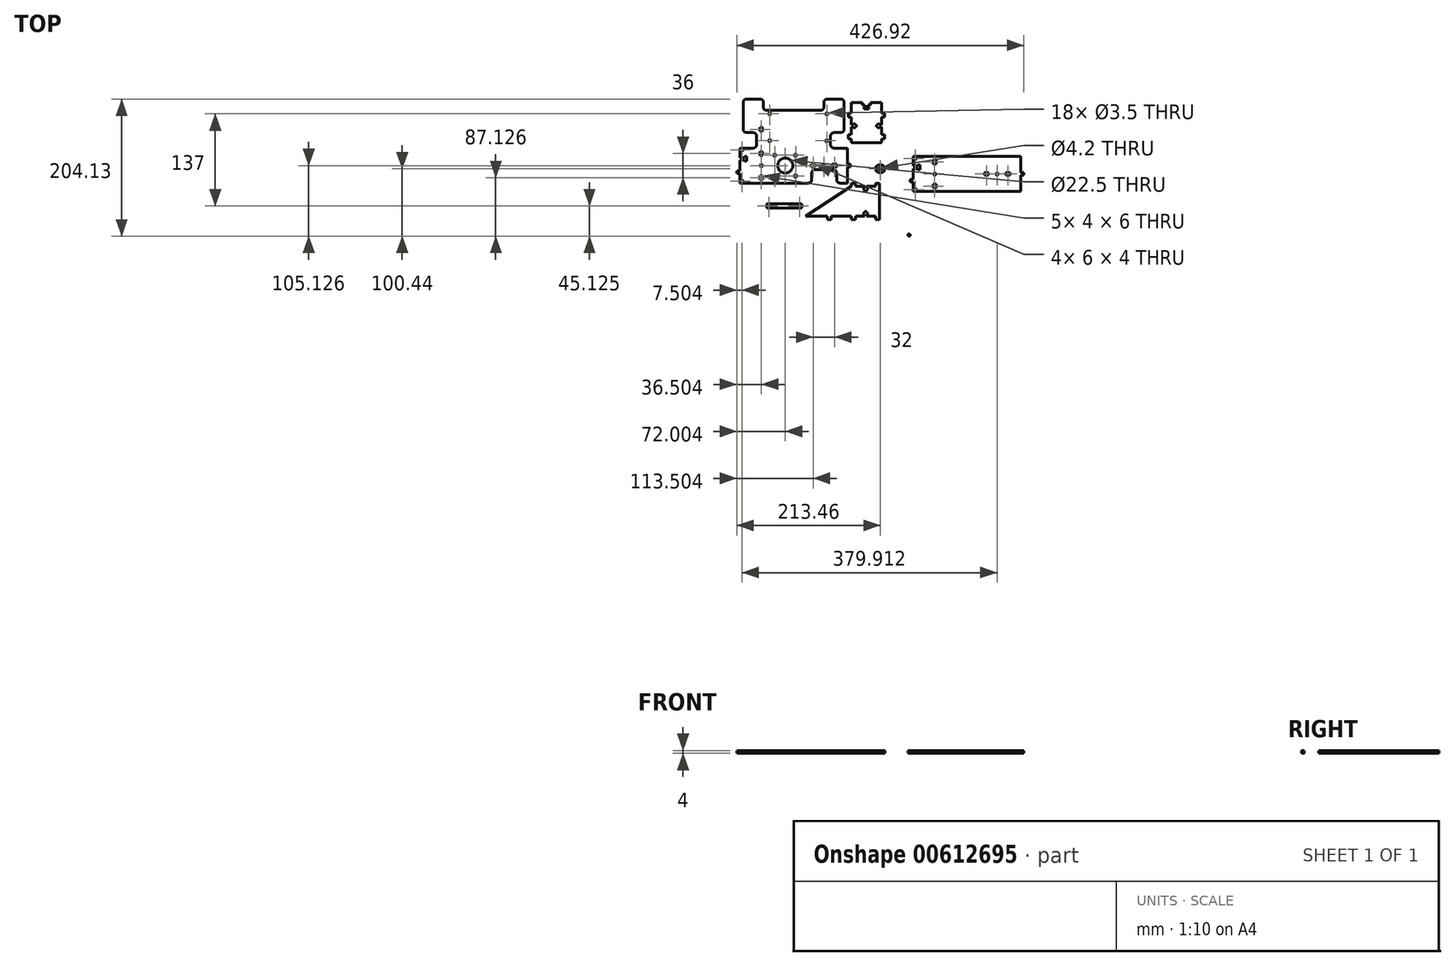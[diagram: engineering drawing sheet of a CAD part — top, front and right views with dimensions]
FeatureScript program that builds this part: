
annotation { "Feature Type Name" : "Feature", "Feature Type Description" : "" }
export const myFeature = defineFeature(function(context is Context, id is Id, definition is map)
    precondition{}
    {
        {
            var Q0;
            Q0=qCreatedBy(makeId("Top.planeOp"),FACE);
            var sketch = newSketch(context, id + "F0", { "sketchPlane" : qUnion([Q0])});
            skLineSegment(sketch, "E0", {"start": v(-0.96, -75.31) * mm, "end": v(-0.96, -21.31) * mm});
            skLineSegment(sketch, "E1", {"start": v(-208.96, 30.69) * mm, "end": v(-188.96, 30.69) * mm});
            skArc(sketch, "E2", {"start": v(-188.96, 30.69) * mm, "mid": v(-185.42, 32.15) * mm, "end": v(-183.96, 35.69) * mm});
            skLineSegment(sketch, "E3", {"start": v(-183.96, 35.69) * mm, "end": v(-183.96, 48.69) * mm});
            skArc(sketch, "E4", {"start": v(-183.96, 48.69) * mm, "mid": v(-185.42, 52.22) * mm, "end": v(-188.96, 53.69) * mm});
            skLineSegment(sketch, "E5", {"start": v(-188.96, 53.69) * mm, "end": v(-198.96, 53.69) * mm});
            skArc(sketch, "E6", {"start": v(-198.96, 53.69) * mm, "mid": v(-202.5, 55.15) * mm, "end": v(-203.96, 58.69) * mm});
            skLineSegment(sketch, "E7", {"start": v(-203.96, 58.69) * mm, "end": v(-203.96, 98.69) * mm});
            skArc(sketch, "E8", {"start": v(-203.96, 98.69) * mm, "mid": v(-202.5, 102.22) * mm, "end": v(-198.96, 103.69) * mm});
            skLineSegment(sketch, "E9", {"start": v(-198.96, 103.69) * mm, "end": v(-178.96, 103.69) * mm});
            skArc(sketch, "E10", {"start": v(-178.96, 103.69) * mm, "mid": v(-175.42, 102.22) * mm, "end": v(-173.96, 98.69) * mm});
            skLineSegment(sketch, "E11", {"start": v(-173.96, 98.69) * mm, "end": v(-173.96, 91.69) * mm});
            skArc(sketch, "E12", {"start": v(-173.96, 91.69) * mm, "mid": v(-172.5, 88.15) * mm, "end": v(-168.96, 86.69) * mm});
            skLineSegment(sketch, "E13", {"start": v(-168.96, 86.69) * mm, "end": v(-88.96, 86.69) * mm});
            skArc(sketch, "E14", {"start": v(-88.96, 86.69) * mm, "mid": v(-85.42, 88.15) * mm, "end": v(-83.96, 91.69) * mm});
            skLineSegment(sketch, "E15", {"start": v(-83.96, 91.69) * mm, "end": v(-83.96, 98.69) * mm});
            skArc(sketch, "E16", {"start": v(-83.96, 98.69) * mm, "mid": v(-82.5, 102.22) * mm, "end": v(-78.96, 103.69) * mm});
            skLineSegment(sketch, "E17", {"start": v(-78.96, 103.69) * mm, "end": v(-58.96, 103.69) * mm});
            skArc(sketch, "E18", {"start": v(-58.96, 103.69) * mm, "mid": v(-55.42, 102.22) * mm, "end": v(-53.96, 98.69) * mm});
            skLineSegment(sketch, "E19", {"start": v(-53.96, 98.69) * mm, "end": v(-53.96, 58.69) * mm});
            skArc(sketch, "E20", {"start": v(-53.96, 58.69) * mm, "mid": v(-55.42, 55.15) * mm, "end": v(-58.96, 53.69) * mm});
            skLineSegment(sketch, "E21", {"start": v(-58.96, 53.69) * mm, "end": v(-68.96, 53.69) * mm});
            skArc(sketch, "E22", {"start": v(-68.96, 53.69) * mm, "mid": v(-72.5, 52.22) * mm, "end": v(-73.96, 48.69) * mm});
            skLineSegment(sketch, "E23", {"start": v(-73.96, 48.69) * mm, "end": v(-73.96, 35.69) * mm});
            skArc(sketch, "E24", {"start": v(-73.96, 35.69) * mm, "mid": v(-72.5, 32.15) * mm, "end": v(-68.96, 30.69) * mm});
            skLineSegment(sketch, "E25", {"start": v(-68.96, 30.69) * mm, "end": v(-48.96, 30.69) * mm});
            skLineSegment(sketch, "E26", {"start": v(-208.96, -7.31) * mm, "end": v(-208.96, -21.31) * mm});
            skLineSegment(sketch, "E27", {"start": v(-208.96, 12.59) * mm, "end": v(-208.96, -3.31) * mm});
            skLineSegment(sketch, "E28", {"start": v(-208.96, 30.69) * mm, "end": v(-208.96, 16.79) * mm});
            skLineSegment(sketch, "E29", {"start": v(48.96, 0.04) * mm, "end": v(48.96, -15.86) * mm});
            skLineSegment(sketch, "E30", {"start": v(48.96, -33.86) * mm, "end": v(48.96, -19.86) * mm});
            skLineSegment(sketch, "E31", {"start": v(48.96, 4.24) * mm, "end": v(48.96, 18.14) * mm});
            skLineSegment(sketch, "E32", {"start": v(-48.96, 2.69) * mm, "end": v(-48.96, -21.31) * mm});
            skLineSegment(sketch, "E33", {"start": v(-48.96, 30.69) * mm, "end": v(-48.96, 6.69) * mm});
            skLineSegment(sketch, "E34", {"start": v(208.96, -5.86) * mm, "end": v(208.96, 18.14) * mm});
            skLineSegment(sketch, "E35", {"start": v(208.96, -33.86) * mm, "end": v(208.96, -9.86) * mm});
            skLineSegment(sketch, "E36", {"start": v(-208.96, -21.31) * mm, "end": v(-106.96, -21.31) * mm});
            skArc(sketch, "E37", {"start": v(-106.96, -21.31) * mm, "mid": v(-103.42, -19.85) * mm, "end": v(-101.96, -16.31) * mm});
            skLineSegment(sketch, "E38", {"start": v(-101.96, -16.31) * mm, "end": v(-101.96, -6.31) * mm});
            skArc(sketch, "E39", {"start": v(-101.96, -6.31) * mm, "mid": v(-100.5, -2.78) * mm, "end": v(-96.96, -1.31) * mm});
            skLineSegment(sketch, "E40", {"start": v(-96.96, -1.31) * mm, "end": v(-69.96, -1.31) * mm});
            skArc(sketch, "E41", {"start": v(-69.96, -1.31) * mm, "mid": v(-66.42, -2.78) * mm, "end": v(-64.96, -6.31) * mm});
            skLineSegment(sketch, "E42", {"start": v(-64.96, -6.31) * mm, "end": v(-64.96, -16.31) * mm});
            skArc(sketch, "E43", {"start": v(-64.96, -16.31) * mm, "mid": v(-63.5, -19.85) * mm, "end": v(-59.96, -21.31) * mm});
            skLineSegment(sketch, "E44", {"start": v(-59.96, -21.31) * mm, "end": v(-48.96, -21.31) * mm});
            skLineSegment(sketch, "E45", {"start": v(48.96, 18.14) * mm, "end": v(208.96, 18.14) * mm});
            skLineSegment(sketch, "E46", {"start": v(-64.96, 6.69) * mm, "end": v(-70.96, 6.69) * mm});
            skLineSegment(sketch, "E47", {"start": v(-96.96, 6.69) * mm, "end": v(-102.96, 6.69) * mm});
            skLineSegment(sketch, "E48", {"start": v(-178.96, 61.69) * mm, "end": v(-178.96, 55.69) * mm});
            skLineSegment(sketch, "E49", {"start": v(-178.96, -10.31) * mm, "end": v(-178.96, -16.31) * mm});
            skLineSegment(sketch, "E50", {"start": v(-178.96, 25.69) * mm, "end": v(-178.96, 19.69) * mm});
            skLineSegment(sketch, "E51", {"start": v(160.96, -9.86) * mm, "end": v(154.96, -9.86) * mm});
            skLineSegment(sketch, "E52", {"start": v(78.96, 7.14) * mm, "end": v(78.96, 13.14) * mm});
            skLineSegment(sketch, "E53", {"start": v(78.96, -28.86) * mm, "end": v(78.96, -22.86) * mm});
            skLineSegment(sketch, "E54", {"start": v(192.96, -9.86) * mm, "end": v(186.96, -9.86) * mm});
            skLineSegment(sketch, "E55", {"start": v(-64.96, 2.69) * mm, "end": v(-70.96, 2.69) * mm});
            skLineSegment(sketch, "E56", {"start": v(-96.96, 2.69) * mm, "end": v(-102.96, 2.69) * mm});
            skLineSegment(sketch, "E57", {"start": v(-174.96, 61.69) * mm, "end": v(-174.96, 55.69) * mm});
            skLineSegment(sketch, "E58", {"start": v(-174.96, -10.31) * mm, "end": v(-174.96, -16.31) * mm});
            skLineSegment(sketch, "E59", {"start": v(-174.96, 25.69) * mm, "end": v(-174.96, 19.69) * mm});
            skLineSegment(sketch, "E60", {"start": v(192.96, -5.86) * mm, "end": v(186.96, -5.86) * mm});
            skLineSegment(sketch, "E61", {"start": v(160.96, -5.86) * mm, "end": v(154.96, -5.86) * mm});
            skLineSegment(sketch, "E62", {"start": v(82.96, 7.14) * mm, "end": v(82.96, 13.14) * mm});
            skLineSegment(sketch, "E63", {"start": v(82.96, -28.86) * mm, "end": v(82.96, -22.86) * mm});
            skLineSegment(sketch, "E64", {"start": v(-64.96, 6.69) * mm, "end": v(-64.96, 2.69) * mm});
            skLineSegment(sketch, "E65", {"start": v(-102.96, 6.69) * mm, "end": v(-102.96, 2.69) * mm});
            skLineSegment(sketch, "E66", {"start": v(-178.96, -16.31) * mm, "end": v(-174.96, -16.31) * mm});
            skLineSegment(sketch, "E67", {"start": v(-178.96, 25.69) * mm, "end": v(-174.96, 25.69) * mm});
            skLineSegment(sketch, "E68", {"start": v(-178.96, 61.69) * mm, "end": v(-174.96, 61.69) * mm});
            skLineSegment(sketch, "E69", {"start": v(-47.46, 82.69) * mm, "end": v(-42.96, 82.69) * mm});
            skLineSegment(sketch, "E70", {"start": v(2.04, 82.69) * mm, "end": v(6.54, 82.69) * mm});
            skLineSegment(sketch, "E71", {"start": v(-42.96, -75.31) * mm, "end": v(-42.96, -70.81) * mm});
            skLineSegment(sketch, "E72", {"start": v(-42.96, -25.81) * mm, "end": v(-42.96, -21.31) * mm});
            skLineSegment(sketch, "E73", {"start": v(-78.96, -75.31) * mm, "end": v(-78.96, -70.81) * mm});
            skLineSegment(sketch, "E74", {"start": v(192.96, -9.86) * mm, "end": v(192.96, -5.86) * mm});
            skLineSegment(sketch, "E75", {"start": v(154.96, -9.86) * mm, "end": v(154.96, -5.86) * mm});
            skLineSegment(sketch, "E76", {"start": v(78.96, 13.14) * mm, "end": v(82.96, 13.14) * mm});
            skLineSegment(sketch, "E77", {"start": v(78.96, -28.86) * mm, "end": v(82.96, -28.86) * mm});
            skLineSegment(sketch, "E78", {"start": v(-70.96, 6.69) * mm, "end": v(-70.96, 2.69) * mm});
            skLineSegment(sketch, "E79", {"start": v(-96.96, 6.69) * mm, "end": v(-96.96, 2.69) * mm});
            skLineSegment(sketch, "E80", {"start": v(-178.96, -10.31) * mm, "end": v(-174.96, -10.31) * mm});
            skLineSegment(sketch, "E81", {"start": v(-178.96, 19.69) * mm, "end": v(-174.96, 19.69) * mm});
            skLineSegment(sketch, "E82", {"start": v(-178.96, 55.69) * mm, "end": v(-174.96, 55.69) * mm});
            skLineSegment(sketch, "E83", {"start": v(-47.46, 76.69) * mm, "end": v(-42.96, 76.69) * mm});
            skLineSegment(sketch, "E84", {"start": v(2.04, 76.69) * mm, "end": v(6.54, 76.69) * mm});
            skLineSegment(sketch, "E85", {"start": v(-6.96, -75.31) * mm, "end": v(-6.96, -70.81) * mm});
            skLineSegment(sketch, "E86", {"start": v(-6.96, -25.81) * mm, "end": v(-6.96, -21.31) * mm});
            skLineSegment(sketch, "E87", {"start": v(-36.96, -75.31) * mm, "end": v(-36.96, -70.81) * mm});
            skLineSegment(sketch, "E88", {"start": v(-36.96, -25.81) * mm, "end": v(-36.96, -21.31) * mm});
            skLineSegment(sketch, "E89", {"start": v(-72.96, -75.31) * mm, "end": v(-72.96, -70.81) * mm});
            skLineSegment(sketch, "E90", {"start": v(186.96, -9.86) * mm, "end": v(186.96, -5.86) * mm});
            skLineSegment(sketch, "E91", {"start": v(160.96, -9.86) * mm, "end": v(160.96, -5.86) * mm});
            skLineSegment(sketch, "E92", {"start": v(78.96, 7.14) * mm, "end": v(82.96, 7.14) * mm});
            skLineSegment(sketch, "E93", {"start": v(78.96, -22.86) * mm, "end": v(82.96, -22.86) * mm});
            skCircle(sketch, "E94", {"center": v(-83.96, 4.69) * mm, "radius": 1.75 * mm});
            skCircle(sketch, "E95", {"center": v(-176.96, 4.69) * mm, "radius": 1.75 * mm});
            skCircle(sketch, "E96", {"center": v(173.96, -7.86) * mm, "radius": 1.75 * mm});
            skCircle(sketch, "E97", {"center": v(80.96, -7.86) * mm, "radius": 1.75 * mm});
            skLineSegment(sketch, "E98", {"start": v(-48.96, 2.69) * mm, "end": v(-44.46, 2.69) * mm});
            skLineSegment(sketch, "E99", {"start": v(208.96, -5.86) * mm, "end": v(213.46, -5.86) * mm});
            skLineSegment(sketch, "E100", {"start": v(-48.96, 6.69) * mm, "end": v(-44.46, 6.69) * mm});
            skLineSegment(sketch, "E101", {"start": v(208.96, -9.86) * mm, "end": v(213.46, -9.86) * mm});
            skLineSegment(sketch, "E102", {"start": v(-44.46, 2.69) * mm, "end": v(-44.46, 6.69) * mm});
            skLineSegment(sketch, "E103", {"start": v(213.46, -5.86) * mm, "end": v(213.46, -9.86) * mm});
            skLineSegment(sketch, "E104", {"start": v(-213.46, -7.31) * mm, "end": v(-208.96, -7.31) * mm});
            skLineSegment(sketch, "E105", {"start": v(44.46, -19.86) * mm, "end": v(48.96, -19.86) * mm});
            skLineSegment(sketch, "E106", {"start": v(-213.46, -3.31) * mm, "end": v(-208.96, -3.31) * mm});
            skLineSegment(sketch, "E107", {"start": v(44.46, -15.86) * mm, "end": v(48.96, -15.86) * mm});
            skLineSegment(sketch, "E108", {"start": v(-213.46, -7.31) * mm, "end": v(-213.46, -3.31) * mm});
            skLineSegment(sketch, "E109", {"start": v(44.46, -19.86) * mm, "end": v(44.46, -15.86) * mm});
            skLineSegment(sketch, "E110", {"start": v(-16.9, 88.69) * mm, "end": v(-24, 88.69) * mm});
            skLineSegment(sketch, "E111", {"start": v(-198.96, 11.14) * mm, "end": v(-198.96, 18.24) * mm});
            skLineSegment(sketch, "E112", {"start": v(58.96, 5.7) * mm, "end": v(58.96, -1.4) * mm});
            skCircle(sketch, "E113", {"center": v(-205.96, -18.31) * mm, "radius": 1.75 * mm});
            skCircle(sketch, "E114", {"center": v(51.96, 15.14) * mm, "radius": 1.75 * mm});
            skCircle(sketch, "E115", {"center": v(-205.96, 27.69) * mm, "radius": 1.75 * mm});
            skCircle(sketch, "E116", {"center": v(51.96, -30.86) * mm, "radius": 1.75 * mm});
            skCircle(sketch, "E117", {"center": v(-156.96, -10.81) * mm, "radius": 1.75 * mm});
            skCircle(sketch, "E118", {"center": v(-156.96, 20.19) * mm, "radius": 1.75 * mm});
            skCircle(sketch, "E119", {"center": v(-125.96, -10.81) * mm, "radius": 1.75 * mm});
            skCircle(sketch, "E120", {"center": v(-125.96, 20.19) * mm, "radius": 1.75 * mm});
            skCircle(sketch, "E121", {"center": v(-141.46, 4.69) * mm, "radius": 11.25 * mm});
            skCircle(sketch, "E122", {"center": v(42.76, -98.69) * mm, "radius": 1.75 * mm});
            skCircle(sketch, "E123", {"center": v(-164.46, 41.69) * mm, "radius": 1.75 * mm});
            skCircle(sketch, "E124", {"center": v(42.76, -58.69) * mm, "radius": 1.75 * mm});
            skCircle(sketch, "E125", {"center": v(-164.46, 81.69) * mm, "radius": 1.75 * mm});
            skCircle(sketch, "E126", {"center": v(127.76, -98.69) * mm, "radius": 1.75 * mm});
            skCircle(sketch, "E127", {"center": v(-79.46, 41.69) * mm, "radius": 1.75 * mm});
            skCircle(sketch, "E128", {"center": v(127.76, -58.69) * mm, "radius": 1.75 * mm});
            skCircle(sketch, "E129", {"center": v(-79.46, 81.69) * mm, "radius": 1.75 * mm});
            skLineSegment(sketch, "E130", {"start": v(-42.96, 38.69) * mm, "end": v(-42.96, 44.69) * mm});
            skLineSegment(sketch, "E131", {"start": v(-42.96, 62.09) * mm, "end": v(-42.96, 50.69) * mm});
            skLineSegment(sketch, "E132", {"start": v(-42.96, 76.69) * mm, "end": v(-42.96, 65.29) * mm});
            skLineSegment(sketch, "E133", {"start": v(-110.96, -70.81) * mm, "end": v(-78.96, -70.81) * mm});
            skLineSegment(sketch, "E134", {"start": v(-20.36, -70.81) * mm, "end": v(-6.96, -70.81) * mm});
            skLineSegment(sketch, "E135", {"start": v(-36.96, -70.81) * mm, "end": v(-23.56, -70.81) * mm});
            skLineSegment(sketch, "E136", {"start": v(-72.96, -70.81) * mm, "end": v(-42.96, -70.81) * mm});
            skLineSegment(sketch, "E137", {"start": v(2.04, 50.69) * mm, "end": v(2.04, 62.09) * mm});
            skLineSegment(sketch, "E138", {"start": v(2.04, 65.29) * mm, "end": v(2.04, 76.69) * mm});
            skLineSegment(sketch, "E139", {"start": v(-6.96, -25.81) * mm, "end": v(-20.36, -25.81) * mm});
            skLineSegment(sketch, "E140", {"start": v(-23.56, -25.81) * mm, "end": v(-36.96, -25.81) * mm});
            skLineSegment(sketch, "E141", {"start": v(6.54, 76.69) * mm, "end": v(6.54, 82.69) * mm});
            skLineSegment(sketch, "E142", {"start": v(-47.46, 82.69) * mm, "end": v(-47.46, 76.69) * mm});
            skLineSegment(sketch, "E143", {"start": v(-0.96, 66.44) * mm, "end": v(-0.96, 65.29) * mm});
            skLineSegment(sketch, "E144", {"start": v(-0.96, 62.09) * mm, "end": v(-0.96, 60.94) * mm});
            skLineSegment(sketch, "E145", {"start": v(-39.96, 66.44) * mm, "end": v(-39.96, 65.29) * mm});
            skLineSegment(sketch, "E146", {"start": v(-39.96, 62.09) * mm, "end": v(-39.96, 60.94) * mm});
            skLineSegment(sketch, "E147", {"start": v(-24.7, -28.81) * mm, "end": v(-23.56, -28.81) * mm});
            skLineSegment(sketch, "E148", {"start": v(-20.36, -28.81) * mm, "end": v(-19.2, -28.81) * mm});
            skLineSegment(sketch, "E149", {"start": v(-24.7, -67.81) * mm, "end": v(-23.56, -67.81) * mm});
            skLineSegment(sketch, "E150", {"start": v(-20.36, -67.81) * mm, "end": v(-19.2, -67.81) * mm});
            skLineSegment(sketch, "E151", {"start": v(-3.56, 66.44) * mm, "end": v(-3.56, 65.29) * mm});
            skLineSegment(sketch, "E152", {"start": v(-3.56, 62.09) * mm, "end": v(-3.56, 60.94) * mm});
            skLineSegment(sketch, "E153", {"start": v(-37.36, 66.44) * mm, "end": v(-37.36, 65.29) * mm});
            skLineSegment(sketch, "E154", {"start": v(-37.36, 62.09) * mm, "end": v(-37.36, 60.94) * mm});
            skLineSegment(sketch, "E155", {"start": v(-24.7, -31.41) * mm, "end": v(-23.56, -31.41) * mm});
            skLineSegment(sketch, "E156", {"start": v(-20.36, -31.41) * mm, "end": v(-19.2, -31.41) * mm});
            skLineSegment(sketch, "E157", {"start": v(-24.7, -65.21) * mm, "end": v(-23.56, -65.21) * mm});
            skLineSegment(sketch, "E158", {"start": v(-20.36, -65.21) * mm, "end": v(-19.2, -65.21) * mm});
            skLineSegment(sketch, "E159", {"start": v(-35.36, 65.29) * mm, "end": v(-35.36, 62.09) * mm});
            skLineSegment(sketch, "E160", {"start": v(-5.56, 65.29) * mm, "end": v(-5.56, 62.09) * mm});
            skLineSegment(sketch, "E161", {"start": v(-23.56, -33.41) * mm, "end": v(-20.36, -33.41) * mm});
            skLineSegment(sketch, "E162", {"start": v(-23.56, -63.21) * mm, "end": v(-20.36, -63.21) * mm});
            skLineSegment(sketch, "E163", {"start": v(-0.96, 60.94) * mm, "end": v(-3.56, 60.94) * mm});
            skLineSegment(sketch, "E164", {"start": v(-39.96, 60.94) * mm, "end": v(-37.36, 60.94) * mm});
            skLineSegment(sketch, "E165", {"start": v(-19.2, -28.81) * mm, "end": v(-19.2, -31.41) * mm});
            skLineSegment(sketch, "E166", {"start": v(-19.2, -67.81) * mm, "end": v(-19.2, -65.21) * mm});
            skLineSegment(sketch, "E167", {"start": v(-39.96, 66.44) * mm, "end": v(-37.36, 66.44) * mm});
            skLineSegment(sketch, "E168", {"start": v(-0.96, 66.44) * mm, "end": v(-3.56, 66.44) * mm});
            skLineSegment(sketch, "E169", {"start": v(-24.7, -67.81) * mm, "end": v(-24.7, -65.21) * mm});
            skLineSegment(sketch, "E170", {"start": v(-24.7, -28.81) * mm, "end": v(-24.7, -31.41) * mm});
            skLineSegment(sketch, "E171", {"start": v(-42.96, -25.81) * mm, "end": v(-110.96, -70.81) * mm});
            skLineSegment(sketch, "E172", {"start": v(-14.46, 98.69) * mm, "end": v(2.04, 98.69) * mm});
            skLineSegment(sketch, "E173", {"start": v(-42.96, 98.69) * mm, "end": v(-26.46, 98.69) * mm});
            skLineSegment(sketch, "E174", {"start": v(2.04, 82.69) * mm, "end": v(2.04, 98.69) * mm});
            skLineSegment(sketch, "E175", {"start": v(-42.96, 82.69) * mm, "end": v(-42.96, 98.69) * mm});
            skLineSegment(sketch, "E176", {"start": v(-47.46, 50.69) * mm, "end": v(-42.96, 50.69) * mm});
            skLineSegment(sketch, "E177", {"start": v(2.04, 50.69) * mm, "end": v(6.54, 50.69) * mm});
            skLineSegment(sketch, "E178", {"start": v(-47.46, 44.69) * mm, "end": v(-42.96, 44.69) * mm});
            skLineSegment(sketch, "E179", {"start": v(2.04, 44.69) * mm, "end": v(6.54, 44.69) * mm});
            skLineSegment(sketch, "E180", {"start": v(6.54, 44.69) * mm, "end": v(6.54, 50.69) * mm});
            skLineSegment(sketch, "E181", {"start": v(-42.96, 38.69) * mm, "end": v(2.04, 38.69) * mm});
            skLineSegment(sketch, "E182", {"start": v(48.96, -33.86) * mm, "end": v(208.96, -33.86) * mm});
            skLineSegment(sketch, "E183", {"start": v(-116.96, -52.31) * mm, "end": v(-116.96, -58.31) * mm});
            skLineSegment(sketch, "E184", {"start": v(-168.96, -52.31) * mm, "end": v(-168.96, -58.31) * mm});
            skCircle(sketch, "E185", {"center": v(-165.96, -55.31) * mm, "radius": 1.75 * mm});
            skCircle(sketch, "E186", {"center": v(-119.96, -55.31) * mm, "radius": 1.75 * mm});
            skLineSegment(sketch, "E187", {"start": v(-47.46, 44.69) * mm, "end": v(-47.46, 50.69) * mm});
            skLineSegment(sketch, "E188", {"start": v(-24, 91.69) * mm, "end": v(-24, 88.69) * mm});
            skLineSegment(sketch, "E189", {"start": v(-201.96, 18.24) * mm, "end": v(-198.96, 18.24) * mm});
            skLineSegment(sketch, "E190", {"start": v(55.96, -1.4) * mm, "end": v(58.96, -1.4) * mm});
            skLineSegment(sketch, "E191", {"start": v(-16.9, 91.69) * mm, "end": v(-16.9, 88.69) * mm});
            skLineSegment(sketch, "E192", {"start": v(-201.96, 11.14) * mm, "end": v(-198.96, 11.14) * mm});
            skLineSegment(sketch, "E193", {"start": v(55.96, 5.7) * mm, "end": v(58.96, 5.7) * mm});
            skLineSegment(sketch, "E194", {"start": v(-16.9, 91.69) * mm, "end": v(-18.36, 91.69) * mm});
            skLineSegment(sketch, "E195", {"start": v(-22.56, 91.69) * mm, "end": v(-24, 91.69) * mm});
            skLineSegment(sketch, "E196", {"start": v(-201.96, 11.14) * mm, "end": v(-201.96, 12.59) * mm});
            skLineSegment(sketch, "E197", {"start": v(-201.96, 16.79) * mm, "end": v(-201.96, 18.24) * mm});
            skLineSegment(sketch, "E198", {"start": v(55.96, 0.04) * mm, "end": v(55.96, -1.4) * mm});
            skLineSegment(sketch, "E199", {"start": v(55.96, 5.7) * mm, "end": v(55.96, 4.24) * mm});
            skLineSegment(sketch, "E200", {"start": v(-22.56, 94.69) * mm, "end": v(-22.56, 91.69) * mm});
            skLineSegment(sketch, "E201", {"start": v(-208.96, 16.79) * mm, "end": v(-201.96, 16.79) * mm});
            skLineSegment(sketch, "E202", {"start": v(48.96, 0.04) * mm, "end": v(55.96, 0.04) * mm});
            skLineSegment(sketch, "E203", {"start": v(-18.36, 94.69) * mm, "end": v(-18.36, 91.69) * mm});
            skLineSegment(sketch, "E204", {"start": v(-208.96, 12.59) * mm, "end": v(-201.96, 12.59) * mm});
            skLineSegment(sketch, "E205", {"start": v(48.96, 4.24) * mm, "end": v(55.96, 4.24) * mm});
            skLineSegment(sketch, "E206", {"start": v(-42.96, 65.29) * mm, "end": v(-39.96, 65.29) * mm});
            skLineSegment(sketch, "E207", {"start": v(-37.36, 65.29) * mm, "end": v(-35.36, 65.29) * mm});
            skLineSegment(sketch, "E208", {"start": v(-37.36, 62.09) * mm, "end": v(-35.36, 62.09) * mm});
            skLineSegment(sketch, "E209", {"start": v(-42.96, 62.09) * mm, "end": v(-39.96, 62.09) * mm});
            skLineSegment(sketch, "E210", {"start": v(-3.56, 65.29) * mm, "end": v(-5.56, 65.29) * mm});
            skLineSegment(sketch, "E211", {"start": v(-3.56, 62.09) * mm, "end": v(-5.56, 62.09) * mm});
            skLineSegment(sketch, "E212", {"start": v(2.04, 62.09) * mm, "end": v(-0.96, 62.09) * mm});
            skLineSegment(sketch, "E213", {"start": v(2.04, 65.29) * mm, "end": v(-0.96, 65.29) * mm});
            skLineSegment(sketch, "E214", {"start": v(-23.56, -25.81) * mm, "end": v(-23.56, -28.81) * mm});
            skLineSegment(sketch, "E215", {"start": v(-20.36, -25.81) * mm, "end": v(-20.36, -28.81) * mm});
            skLineSegment(sketch, "E216", {"start": v(-20.36, -31.41) * mm, "end": v(-20.36, -33.41) * mm});
            skLineSegment(sketch, "E217", {"start": v(-23.56, -31.41) * mm, "end": v(-23.56, -33.41) * mm});
            skLineSegment(sketch, "E218", {"start": v(-23.56, -65.21) * mm, "end": v(-23.56, -63.21) * mm});
            skLineSegment(sketch, "E219", {"start": v(-20.36, -65.21) * mm, "end": v(-20.36, -63.21) * mm});
            skLineSegment(sketch, "E220", {"start": v(-20.36, -70.81) * mm, "end": v(-20.36, -67.81) * mm});
            skLineSegment(sketch, "E221", {"start": v(-23.56, -70.81) * mm, "end": v(-23.56, -67.81) * mm});
            skArc(sketch, "E222", {"start": v(132.76, -58.69) * mm, "mid": v(131.3, -55.15) * mm, "end": v(127.76, -53.69) * mm});
            skLineSegment(sketch, "E223", {"start": v(127.76, -53.69) * mm, "end": v(42.76, -53.69) * mm});
            skArc(sketch, "E224", {"start": v(42.76, -53.69) * mm, "mid": v(39.23, -55.15) * mm, "end": v(37.76, -58.69) * mm});
            skLineSegment(sketch, "E225", {"start": v(37.76, -58.69) * mm, "end": v(37.76, -98.69) * mm});
            skArc(sketch, "E226", {"start": v(37.76, -98.69) * mm, "mid": v(39.23, -102.22) * mm, "end": v(42.76, -103.69) * mm});
            skArc(sketch, "E227", {"start": v(47.71, -59.4) * mm, "mid": v(48.38, -58.17) * mm, "end": v(49.69, -57.69) * mm});
            skLineSegment(sketch, "E228", {"start": v(49.69, -57.69) * mm, "end": v(120.83, -57.69) * mm});
            skArc(sketch, "E229", {"start": v(120.83, -57.69) * mm, "mid": v(122.14, -58.17) * mm, "end": v(122.81, -59.4) * mm});
            skArc(sketch, "E230", {"start": v(122.81, -59.4) * mm, "mid": v(124.77, -62.69) * mm, "end": v(128.48, -63.63) * mm});
            skArc(sketch, "E231", {"start": v(128.48, -63.63) * mm, "mid": v(130.07, -64.1) * mm, "end": v(130.76, -65.61) * mm});
            skLineSegment(sketch, "E232", {"start": v(130.76, -65.61) * mm, "end": v(130.76, -78.69) * mm});
            skArc(sketch, "E233", {"start": v(130.76, -78.69) * mm, "mid": v(129.35, -79.27) * mm, "end": v(128.76, -80.69) * mm});
            skLineSegment(sketch, "E234", {"start": v(128.76, -80.69) * mm, "end": v(128.76, -91.76) * mm});
            skArc(sketch, "E235", {"start": v(128.76, -91.76) * mm, "mid": v(128.27, -93.07) * mm, "end": v(127.05, -93.74) * mm});
            skArc(sketch, "E236", {"start": v(127.05, -93.74) * mm, "mid": v(124.23, -95.15) * mm, "end": v(122.81, -97.97) * mm});
            skArc(sketch, "E237", {"start": v(122.81, -97.97) * mm, "mid": v(122.14, -99.2) * mm, "end": v(120.83, -99.69) * mm});
            skLineSegment(sketch, "E238", {"start": v(120.83, -99.69) * mm, "end": v(49.69, -99.69) * mm});
            skArc(sketch, "E239", {"start": v(49.69, -99.69) * mm, "mid": v(48.38, -99.2) * mm, "end": v(47.71, -97.97) * mm});
            skArc(sketch, "E240", {"start": v(47.71, -97.97) * mm, "mid": v(46.3, -95.15) * mm, "end": v(43.48, -93.74) * mm});
            skArc(sketch, "E241", {"start": v(43.48, -93.74) * mm, "mid": v(42.25, -93.07) * mm, "end": v(41.76, -91.76) * mm});
            skLineSegment(sketch, "E242", {"start": v(41.76, -91.76) * mm, "end": v(41.76, -65.61) * mm});
            skArc(sketch, "E243", {"start": v(41.76, -65.61) * mm, "mid": v(42.25, -64.3) * mm, "end": v(43.48, -63.63) * mm});
            skArc(sketch, "E244", {"start": v(43.48, -63.63) * mm, "mid": v(46.3, -62.22) * mm, "end": v(47.71, -59.4) * mm});
            skArc(sketch, "E245", {"start": v(127.76, -103.69) * mm, "mid": v(131.3, -102.22) * mm, "end": v(132.76, -98.69) * mm});
            skLineSegment(sketch, "E246", {"start": v(132.76, -98.69) * mm, "end": v(132.76, -58.69) * mm});
            skLineSegment(sketch, "E247", {"start": v(-6.96, -75.31) * mm, "end": v(-0.96, -75.31) * mm});
            skLineSegment(sketch, "E248", {"start": v(-78.96, -75.31) * mm, "end": v(-72.96, -75.31) * mm});
            skLineSegment(sketch, "E249", {"start": v(-42.96, -75.31) * mm, "end": v(-36.96, -75.31) * mm});
            skLineSegment(sketch, "E250", {"start": v(-168.96, -52.31) * mm, "end": v(-116.96, -52.31) * mm});
            skLineSegment(sketch, "E251", {"start": v(-168.96, -58.31) * mm, "end": v(-116.96, -58.31) * mm});
            skLineSegment(sketch, "E252", {"start": v(2.04, 44.69) * mm, "end": v(2.04, 38.69) * mm});
            skLineSegment(sketch, "E253", {"start": v(-42.96, -21.31) * mm, "end": v(-36.96, -21.31) * mm});
            skLineSegment(sketch, "E254", {"start": v(-6.96, -21.31) * mm, "end": v(-0.96, -21.31) * mm});
            skLineSegment(sketch, "E255", {"start": v(42.76, -103.69) * mm, "end": v(127.76, -103.69) * mm});
            skLineSegment(sketch, "E256", {"start": v(-26.46, 98.69) * mm, "end": v(-26.46, 94.69) * mm});
            skLineSegment(sketch, "E257", {"start": v(-26.46, 94.69) * mm, "end": v(-22.56, 94.69) * mm});
            skLineSegment(sketch, "E258", {"start": v(-14.46, 94.69) * mm, "end": v(-14.46, 98.69) * mm});
            skLineSegment(sketch, "E259.trimOffspring", {"start": v(-18.36, 94.69) * mm, "end": v(-14.46, 94.69) * mm});
            skCircle(sketch, "E260", {"center": v(0, 0) * mm, "radius": 2.1 * mm});
            skLineSegment(sketch, "E261", {"start": v(-7, 2) * mm, "end": v(-6, 2) * mm});
            skLineSegment(sketch, "E262", {"start": v(-6, 2) * mm, "end": v(-6, -2) * mm});
            skLineSegment(sketch, "E263", {"start": v(-6, -2) * mm, "end": v(-7, -2) * mm});
            skLineSegment(sketch, "E264", {"start": v(7, 2) * mm, "end": v(6, 2) * mm});
            skLineSegment(sketch, "E265", {"start": v(6, 2) * mm, "end": v(6, -2) * mm});
            skLineSegment(sketch, "E266", {"start": v(6, -2) * mm, "end": v(7, -2) * mm});
            skLineSegment(sketch, "E267", {"start": v(-6, 0) * mm, "end": v(0, 0) * mm, "construction": true});
            skLineSegment(sketch, "E268", {"start": v(6, 0) * mm, "end": v(0, 0) * mm, "construction": true});
            skArc(sketch, "E269", {"start": v(7, 2) * mm, "mid": v(0, 6) * mm, "end": v(-7, 2) * mm});
            skArc(sketch, "E270", {"start": v(-7, -2) * mm, "mid": v(0, -6) * mm, "end": v(7, -2) * mm});
            skCircle(sketch, "E271", {"center": v(0, 0) * mm, "radius": 6 * mm, "construction": true});
            skSolve(sketch);
        }
        {
            var Q0;
            Q0=makeQuery(id+"F0.imprint","IMPRINT",FACE,{"disambiguationData":[TD([[makeQuery(id+"F0.imprint","IMPRINT",EDGE,{"derivedFrom":sQuery(id+"F0.wireOp",EDGE,"E1")}),-1.0]])]});
            var Q1;
            Q1=makeQuery(id+"F0.imprint","IMPRINT",FACE,{"disambiguationData":[TD([[makeQuery(id+"F0.imprint","IMPRINT",EDGE,{"derivedFrom":sQuery(id+"F0.wireOp",EDGE,"E183")}),-1.0]])]});
            var Q2;
            Q2=makeQuery(id+"F0.imprint","IMPRINT",FACE,{"disambiguationData":[TD([[makeQuery(id+"F0.imprint","IMPRINT",EDGE,{"derivedFrom":sQuery(id+"F0.wireOp",EDGE,"E0")}),1.0]])]});
            var Q3;
            Q3=makeQuery(id+"F0.imprint","IMPRINT",FACE,{"disambiguationData":[TD([[makeQuery(id+"F0.imprint","IMPRINT",EDGE,{"derivedFrom":sQuery(id+"F0.wireOp",EDGE,"E69")}),-1.0]])]});
            var Q4;
            Q4=makeQuery(id+"F0.imprint","IMPRINT",FACE,{"disambiguationData":[TD([[makeQuery(id+"F0.imprint","IMPRINT",EDGE,{"derivedFrom":sQuery(id+"F0.wireOp",EDGE,"E29")}),1.0]])]});
            var Q5;
            Q5=makeQuery(id+"F0.imprint","IMPRINT",FACE,{"disambiguationData":[TD([[makeQuery(id+"F0.imprint","IMPRINT",EDGE,{"derivedFrom":sQuery(id+"F0.wireOp",EDGE,"E122")}),1.0]])]});
            var Q6;
            Q6=makeQuery(id+"F0.imprint","IMPRINT",FACE,{"disambiguationData":[TD([[makeQuery(id+"F0.imprint","IMPRINT",EDGE,{"derivedFrom":sQuery(id+"F0.wireOp",EDGE,"E260")}),-1.0]])]});
            extrude(context, id + "F1", {"entities" : qUnion([Q0, Q1, Q2, Q3, Q4, Q5, Q6]), "depth" : 4 * mm, "offsetDistance" : 25 * mm});
        }
    });
